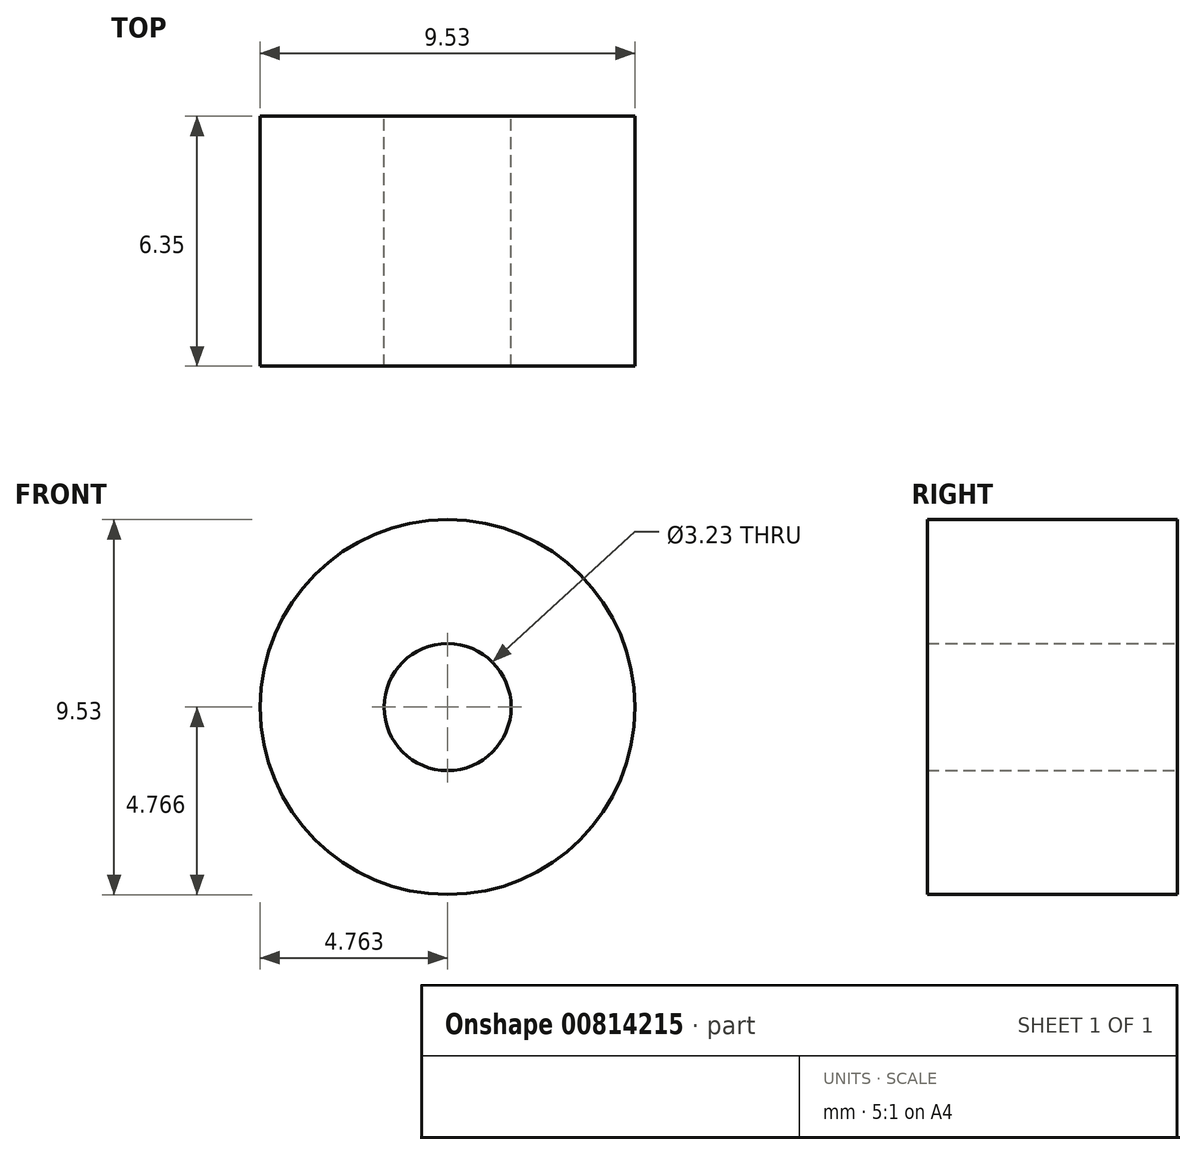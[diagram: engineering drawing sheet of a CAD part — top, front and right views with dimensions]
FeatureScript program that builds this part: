
annotation { "Feature Type Name" : "Feature", "Feature Type Description" : "" }
export const myFeature = defineFeature(function(context is Context, id is Id, definition is map)
    precondition{}
    {
        {
            var Q0;
            Q0=qCreatedBy(makeId("Front.planeOp"),FACE);
            var sketch = newSketch(context, id + "F0", { "sketchPlane" : qUnion([Q0])});
            skCircle(sketch, "E0", {"center": v(-50.47, 38.23) * mm, "radius": 4.76 * mm});
            skCircle(sketch, "E1", {"center": v(-50.47, 38.23) * mm, "radius": 1.61 * mm});
            skSolve(sketch);
        }
        {
            var Q0;
            Q0=makeQuery(id+"F0.imprint","IMPRINT",FACE,{"disambiguationData":[TD([[makeQuery(id+"F0.imprint","IMPRINT",EDGE,{"derivedFrom":sQuery(id+"F0.wireOp",EDGE,"E0")}),1.0]])]});
            extrude(context, id + "F1", {"entities" : qUnion([Q0]), "depth" : 6.35 * mm, "offsetDistance" : 25.4 * mm});
        }
    });
